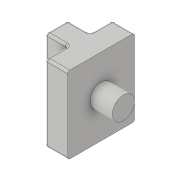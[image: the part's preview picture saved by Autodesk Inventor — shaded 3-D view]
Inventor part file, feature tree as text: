
AUTODESK INVENTOR PART (.ipt)
format: ipt  version: 2017 (Build 210142000, 142)  size: 142,336 bytes
history: native  units: in
note: dims shown in document units (in); Inventor stores cm internally (conversion verified against a paired STEP export)
features: extrude x2, fillet x2, sketch x2
ambient origin geometry x8: Origin, YZ Plane, XZ Plane, XY Plane, X Axis, Y Axis, Z Axis, Center Point
bodies: Solid1 (feature_tree)
feature tree (6):
  extrude  "Extrusion1"  Depth=0.4in
  extrude  "Extrusion2"  Depth=0.6in
  fillet  "Fillet1"  Radius=0.4in
  fillet  "Fillet2"  Radius=1.38in
  sketch  "Sketch1"  dims[d1=0.4in d2=0.4in]
  sketch  "Sketch2"  dims[d3=0.4in d4=0.6in d5=0.4in d6=1.38in d7=0.0in d8=0.4in d9=0.4in d10=0.0in d11=0.04in d12=0.04in]
